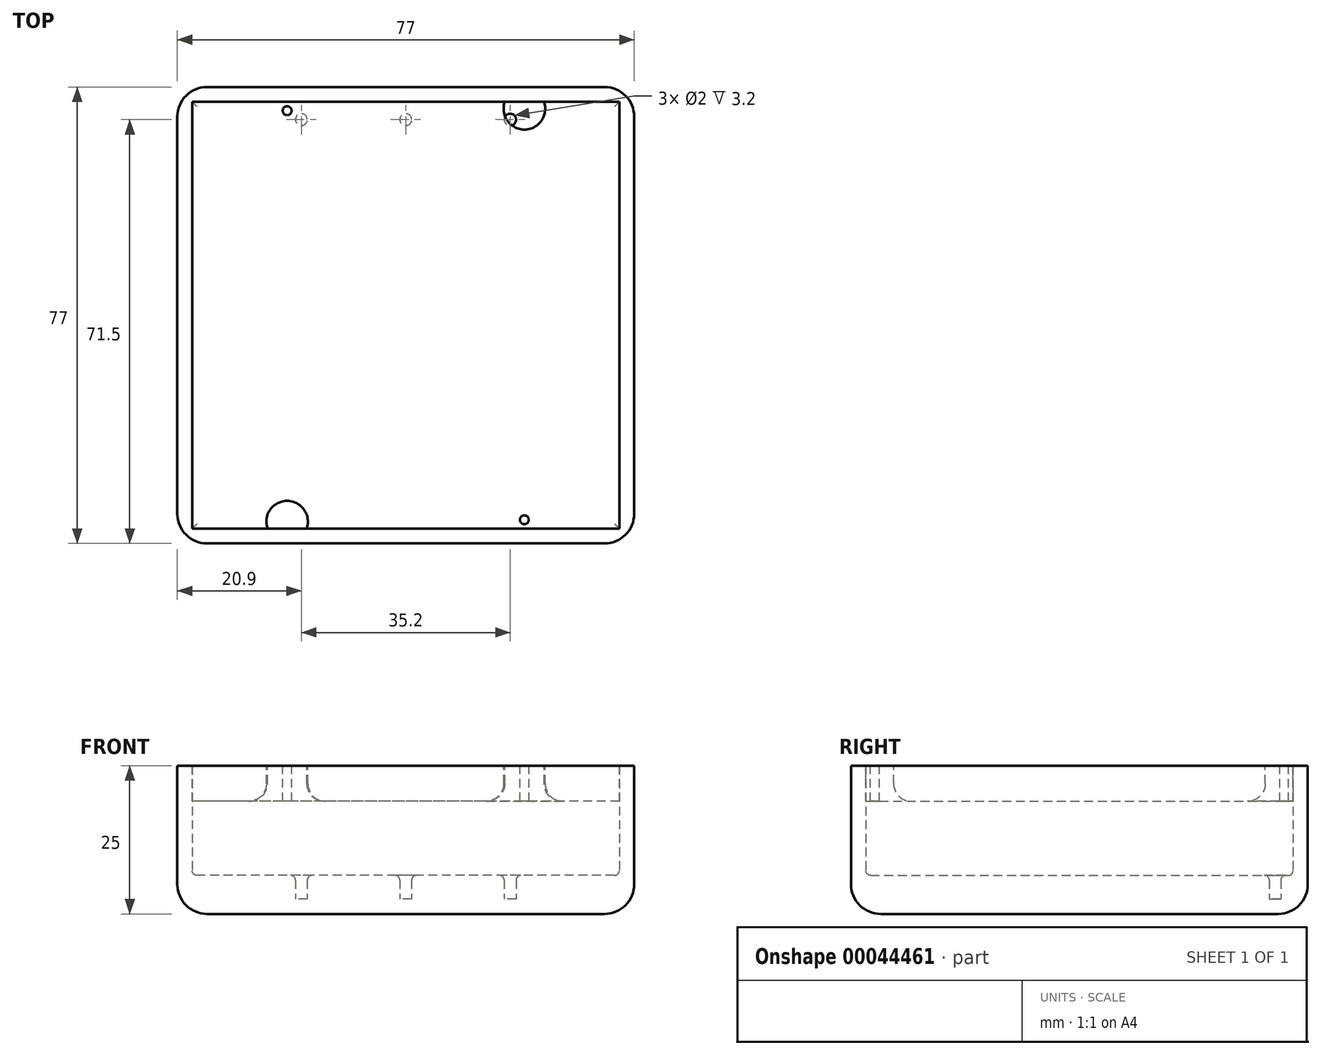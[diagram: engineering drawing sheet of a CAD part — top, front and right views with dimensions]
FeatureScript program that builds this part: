
annotation { "Feature Type Name" : "Feature", "Feature Type Description" : "" }
export const myFeature = defineFeature(function(context is Context, id is Id, definition is map)
    precondition{}
    {
        {
            var Q0;
            Q0=qCreatedBy(makeId("Top.planeOp"),FACE);
            var sketch = newSketch(context, id + "F0", { "sketchPlane" : qUnion([Q0])});
            skLineSegment(sketch, "E0.rect.bottom", {"start": v(38.5, -38.5) * mm, "end": v(-38.5, -38.5) * mm});
            skLineSegment(sketch, "E0.rect.top", {"start": v(38.5, 38.5) * mm, "end": v(-38.5, 38.5) * mm});
            skLineSegment(sketch, "E0.rect.left", {"start": v(38.5, -38.5) * mm, "end": v(38.5, 38.5) * mm});
            skLineSegment(sketch, "E0.rect.right", {"start": v(-38.5, -38.5) * mm, "end": v(-38.5, 38.5) * mm});
            skPoint(sketch, "E0.rect.middle", {"position": v(0, 0) * mm});
            skSolve(sketch);
        }
        {
            var Q0;
            Q0 = qSketchRegion(id + "F0", true);
            extrude(context, id + "F1", {"entities" : qUnion([Q0]), "depth" : 25 * mm});
        }
        {
            var Q0;
            Q0=makeQuery(id+"F1.opExtrude","CAP_FACE",FACE,{"disambiguationData":[OSD([sQuery(id+"F0.wireOp",EDGE,"E0.rect.bottom"),sQuery(id+"F0.wireOp",EDGE,"E0.rect.top"),sQuery(id+"F0.wireOp",EDGE,"E0.rect.left"),sQuery(id+"F0.wireOp",EDGE,"E0.rect.right")])],"isStart":false});
            shell(context, id + "F2", {"entities" : qUnion([Q0]), "thickness" : 2.5 * mm});
        }
        {
            var Q0;
            Q0=makeQuery(id+"F1.opExtrude","CAP_FACE",FACE,{"disambiguationData":[OSD([sQuery(id+"F0.wireOp",EDGE,"E0.rect.bottom"),sQuery(id+"F0.wireOp",EDGE,"E0.rect.top"),sQuery(id+"F0.wireOp",EDGE,"E0.rect.left"),sQuery(id+"F0.wireOp",EDGE,"E0.rect.right")])],"isStart":true});
            var Q1;
            Q1=makeQuery(id+"F1.opExtrude","SWEPT_EDGE",EDGE,{"disambiguationData":[OSD([sQuery(id+"F0.wireOp",EDGE,"E0.rect.bottom"),sQuery(id+"F0.wireOp",EDGE,"E0.rect.right")])]});
            var Q2;
            Q2=makeQuery(id+"F1.opExtrude","SWEPT_EDGE",EDGE,{"disambiguationData":[OSD([sQuery(id+"F0.wireOp",EDGE,"E0.rect.bottom"),sQuery(id+"F0.wireOp",EDGE,"E0.rect.left")])]});
            var Q3;
            Q3=makeQuery(id+"F1.opExtrude","SWEPT_EDGE",EDGE,{"disambiguationData":[OSD([sQuery(id+"F0.wireOp",EDGE,"E0.rect.top"),sQuery(id+"F0.wireOp",EDGE,"E0.rect.left")])]});
            var Q4;
            Q4=makeQuery(id+"F1.opExtrude","SWEPT_EDGE",EDGE,{"disambiguationData":[OSD([sQuery(id+"F0.wireOp",EDGE,"E0.rect.top"),sQuery(id+"F0.wireOp",EDGE,"E0.rect.right")])]});
            fillet(context, id + "F3", {"entities" : qUnion([Q0, Q1, Q2, Q3, Q4]), "radius" : 5 * mm, "tangentPropagation" : true, "allowEdgeOverflow" : false});
        }
        {
            var Q0;
            Q0=makeQuery(id+"F2.opShell","OFFSET_FACE",FACE,{"disambiguationData":[OSD([sQuery(id+"F0.wireOp",EDGE,"E0.rect.bottom"),sQuery(id+"F0.wireOp",EDGE,"E0.rect.top"),sQuery(id+"F0.wireOp",EDGE,"E0.rect.left"),sQuery(id+"F0.wireOp",EDGE,"E0.rect.right")])]});
            var sketch = newSketch(context, id + "F4", { "sketchPlane" : qUnion([Q0])});
            skCircle(sketch, "E1", {"center": v(0, -33) * mm, "radius": 1 * mm});
            skCircle(sketch, "E2", {"center": v(-17.6, -33) * mm, "radius": 1 * mm});
            skCircle(sketch, "E3", {"center": v(17.6, -33) * mm, "radius": 1 * mm});
            skCircle(sketch, "E4.MirrorC", {"center": v(17.6, 33) * mm, "radius": 1 * mm});
            skCircle(sketch, "E5.MirrorC", {"center": v(0, 33) * mm, "radius": 1 * mm});
            skCircle(sketch, "E6.MirrorC", {"center": v(-17.6, 33) * mm, "radius": 1 * mm});
            skSolve(sketch);
        }
        {
            var Q0;
            Q0=makeQuery(id+"F4.imprint","IMPRINT",FACE,{"disambiguationData":[TD([[makeQuery(id+"F4.imprint","IMPRINT",EDGE,{"derivedFrom":sQuery(id+"F4.wireOp",EDGE,"E4.MirrorC")}),-1.0]])]});
            var Q1;
            Q1=makeQuery(id+"F4.imprint","IMPRINT",FACE,{"disambiguationData":[TD([[makeQuery(id+"F4.imprint","IMPRINT",EDGE,{"derivedFrom":sQuery(id+"F4.wireOp",EDGE,"E3")}),1.0]])]});
            var Q2;
            Q2=makeQuery(id+"F4.imprint","IMPRINT",FACE,{"disambiguationData":[TD([[makeQuery(id+"F4.imprint","IMPRINT",EDGE,{"derivedFrom":sQuery(id+"F4.wireOp",EDGE,"E1")}),1.0]])]});
            var Q3;
            Q3=makeQuery(id+"F4.imprint","IMPRINT",FACE,{"disambiguationData":[TD([[makeQuery(id+"F4.imprint","IMPRINT",EDGE,{"derivedFrom":sQuery(id+"F4.wireOp",EDGE,"E5.MirrorC")}),-1.0]])]});
            var Q4;
            Q4=makeQuery(id+"F4.imprint","IMPRINT",FACE,{"disambiguationData":[TD([[makeQuery(id+"F4.imprint","IMPRINT",EDGE,{"derivedFrom":sQuery(id+"F4.wireOp",EDGE,"E6.MirrorC")}),-1.0]])]});
            var Q5;
            Q5=makeQuery(id+"F4.imprint","IMPRINT",FACE,{"disambiguationData":[TD([[makeQuery(id+"F4.imprint","IMPRINT",EDGE,{"derivedFrom":sQuery(id+"F4.wireOp",EDGE,"E2")}),1.0]])]});
            extrude(context, id + "F5", {"entities" : qUnion([Q0, Q1, Q2, Q3, Q4, Q5]), "operationType" : NewBodyOperationType.ADD, "depth" : 4 * mm});
        }
        {
            var Q0;
            Q0=makeQuery(id+"F1.opExtrude","CAP_FACE",FACE,{"disambiguationData":[OSD([sQuery(id+"F0.wireOp",EDGE,"E0.rect.bottom"),sQuery(id+"F0.wireOp",EDGE,"E0.rect.top"),sQuery(id+"F0.wireOp",EDGE,"E0.rect.left"),sQuery(id+"F0.wireOp",EDGE,"E0.rect.right")])],"isStart":false});
            var sketch = newSketch(context, id + "F6", { "sketchPlane" : qUnion([Q0])});
            skArc(sketch, "E7", {"start": v(-23.3, 36) * mm, "mid": v(-20, 31.32) * mm, "end": v(-16.7, 36) * mm});
            skArc(sketch, "E8.MirrorCS", {"start": v(23.3, 36) * mm, "mid": v(20, 31.32) * mm, "end": v(16.7, 36) * mm});
            skArc(sketch, "E9.MirrorCS", {"start": v(-23.3, -36) * mm, "mid": v(-20, -31.32) * mm, "end": v(-16.7, -36) * mm});
            skArc(sketch, "E10.MirrorCS", {"start": v(23.3, -36) * mm, "mid": v(20, -31.32) * mm, "end": v(16.7, -36) * mm});
            skLineSegment(sketch, "E11", {"start": v(-23.3, 36) * mm, "end": v(-16.7, 36) * mm});
            skLineSegment(sketch, "E12", {"start": v(16.7, 36) * mm, "end": v(23.3, 36) * mm});
            skLineSegment(sketch, "E13", {"start": v(-23.3, -36) * mm, "end": v(-16.7, -36) * mm});
            skLineSegment(sketch, "E14", {"start": v(16.7, -36) * mm, "end": v(23.3, -36) * mm});
            skSolve(sketch);
        }
        {
            var Q0;
            Q0=makeQuery(id+"F6.imprint","IMPRINT",FACE,{"disambiguationData":[TD([[makeQuery(id+"F6.imprint","IMPRINT",EDGE,{"derivedFrom":sQuery(id+"F6.wireOp",EDGE,"E9.MirrorCS")}),-1.0]])]});
            var Q1;
            Q1=makeQuery(id+"F6.imprint","IMPRINT",FACE,{"disambiguationData":[TD([[makeQuery(id+"F6.imprint","IMPRINT",EDGE,{"derivedFrom":sQuery(id+"F6.wireOp",EDGE,"E10.MirrorCS")}),1.0]])]});
            var Q2;
            Q2=makeQuery(id+"F6.imprint","IMPRINT",FACE,{"disambiguationData":[TD([[makeQuery(id+"F6.imprint","IMPRINT",EDGE,{"derivedFrom":sQuery(id+"F6.wireOp",EDGE,"E7")}),1.0]])]});
            var Q3;
            Q3=makeQuery(id+"F6.imprint","IMPRINT",FACE,{"disambiguationData":[TD([[makeQuery(id+"F6.imprint","IMPRINT",EDGE,{"derivedFrom":sQuery(id+"F6.wireOp",EDGE,"E8.MirrorCS")}),-1.0]])]});
            extrude(context, id + "F7", {"entities" : qUnion([Q0, Q1, Q2, Q3]), "oppositeDirection" : true, "depth" : 6 * mm});
        }
        {
            var Q0;
            Q0=makeQuery(id+"F7.opExtrude","CAP_EDGE",EDGE,{"disambiguationData":[OSD([sQuery(id+"F6.wireOp",EDGE,"E9.MirrorCS")])],"isStart":false});
            var Q1;
            Q1=makeQuery(id+"F7.opExtrude","CAP_EDGE",EDGE,{"disambiguationData":[OSD([sQuery(id+"F6.wireOp",EDGE,"E10.MirrorCS")])],"isStart":false});
            var Q2;
            Q2=makeQuery(id+"F7.opExtrude","CAP_EDGE",EDGE,{"disambiguationData":[OSD([sQuery(id+"F6.wireOp",EDGE,"E7")])],"isStart":false});
            var Q3;
            Q3=makeQuery(id+"F7.opExtrude","CAP_EDGE",EDGE,{"disambiguationData":[OSD([sQuery(id+"F6.wireOp",EDGE,"E8.MirrorCS")])],"isStart":false});
            fillet(context, id + "F8", {"entities" : qUnion([Q0, Q1, Q2, Q3]), "radius" : 3 * mm, "tangentPropagation" : true, "allowEdgeOverflow" : false});
        }
        {
            var Q0;
            Q0=makeQuery(id+"F1.opExtrude","CAP_FACE",FACE,{"disambiguationData":[OSD([sQuery(id+"F0.wireOp",EDGE,"E0.rect.bottom"),sQuery(id+"F0.wireOp",EDGE,"E0.rect.top"),sQuery(id+"F0.wireOp",EDGE,"E0.rect.left"),sQuery(id+"F0.wireOp",EDGE,"E0.rect.right")])],"isStart":false});
            var sketch = newSketch(context, id + "F9", { "sketchPlane" : qUnion([Q0])});
            skCircle(sketch, "E15", {"center": v(-20, 34.5) * mm, "radius": 0.75 * mm});
            skCircle(sketch, "E16.MirrorC", {"center": v(-20, -34.5) * mm, "radius": 0.75 * mm});
            skCircle(sketch, "E17.MirrorC", {"center": v(20, 34.5) * mm, "radius": 0.75 * mm});
            skCircle(sketch, "E18.MirrorC", {"center": v(20, -34.5) * mm, "radius": 0.75 * mm});
            skSolve(sketch);
        }
        {
            var Q0;
            Q0 = qSketchRegion(id + "F9", true);
            extrude(context, id + "F10", {"entities" : qUnion([Q0]), "operationType" : NewBodyOperationType.REMOVE, "endBound" : BoundingType.UP_TO_NEXT, "oppositeDirection" : true, "depth" : 25 * mm});
        }
        {
            var Q0;
            Q0=makeQuery(id+"F5.opExtrude","CAP_EDGE",EDGE,{"disambiguationData":[OSD([sQuery(id+"F4.wireOp",EDGE,"E2")])],"isStart":false});
            var Q1;
            Q1=makeQuery(id+"F5.opExtrude","CAP_EDGE",EDGE,{"disambiguationData":[OSD([sQuery(id+"F4.wireOp",EDGE,"E1")])],"isStart":false});
            var Q2;
            Q2=makeQuery(id+"F5.opExtrude","CAP_EDGE",EDGE,{"disambiguationData":[OSD([sQuery(id+"F4.wireOp",EDGE,"E3")])],"isStart":false});
            var Q3;
            Q3=makeQuery(id+"F5.opExtrude","CAP_EDGE",EDGE,{"disambiguationData":[OSD([sQuery(id+"F4.wireOp",EDGE,"E6.MirrorC")])],"isStart":false});
            var Q4;
            Q4=makeQuery(id+"F5.opExtrude","CAP_FACE",FACE,{"disambiguationData":[OSD([sQuery(id+"F4.wireOp",EDGE,"E5.MirrorC")])],"isStart":false});
            var Q5;
            Q5=makeQuery(id+"F5.opExtrude","CAP_EDGE",EDGE,{"disambiguationData":[OSD([sQuery(id+"F4.wireOp",EDGE,"E4.MirrorC")])],"isStart":false});
            fillet(context, id + "F11", {"entities" : qUnion([Q0, Q1, Q2, Q3, Q4, Q5]), "radius" : .8 * mm, "tangentPropagation" : true, "allowEdgeOverflow" : false});
        }
    });
